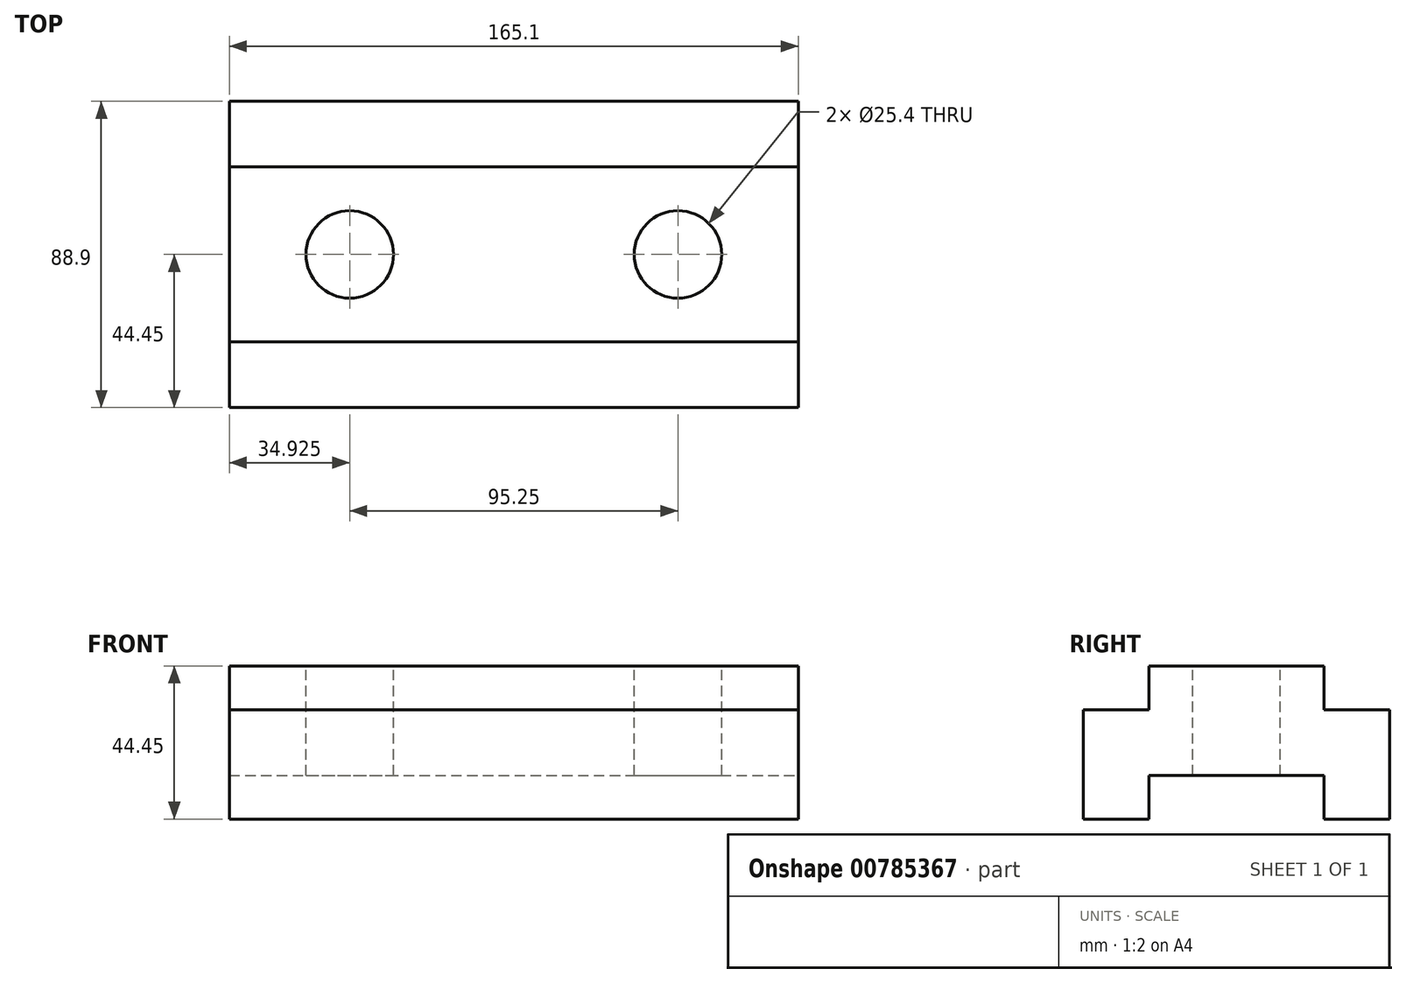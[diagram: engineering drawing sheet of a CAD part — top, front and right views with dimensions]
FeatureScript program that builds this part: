
annotation { "Feature Type Name" : "Feature", "Feature Type Description" : "" }
export const myFeature = defineFeature(function(context is Context, id is Id, definition is map)
    precondition{}
    {
        {
            var Q0;
            Q0=qCreatedBy(makeId("Right.planeOp"),FACE);
            var sketch = newSketch(context, id + "F0", { "sketchPlane" : qUnion([Q0])});
            skLineSegment(sketch, "E0", {"start": v(0, 0) * mm, "end": v(19.05, 0) * mm});
            skLineSegment(sketch, "E1", {"start": v(19.05, 0) * mm, "end": v(19.05, 12.7) * mm});
            skLineSegment(sketch, "E2", {"start": v(19.05, 12.7) * mm, "end": v(69.85, 12.7) * mm});
            skLineSegment(sketch, "E3", {"start": v(69.85, 12.7) * mm, "end": v(69.85, 0) * mm});
            skLineSegment(sketch, "E4", {"start": v(69.85, 0) * mm, "end": v(88.9, 0) * mm});
            skLineSegment(sketch, "E5", {"start": v(88.9, 0) * mm, "end": v(88.9, 31.75) * mm});
            skLineSegment(sketch, "E6", {"start": v(88.9, 31.75) * mm, "end": v(69.85, 31.75) * mm});
            skLineSegment(sketch, "E7", {"start": v(69.85, 31.75) * mm, "end": v(69.85, 44.45) * mm});
            skLineSegment(sketch, "E8", {"start": v(69.85, 44.45) * mm, "end": v(19.05, 44.45) * mm});
            skLineSegment(sketch, "E9", {"start": v(19.05, 44.45) * mm, "end": v(19.05, 31.75) * mm});
            skLineSegment(sketch, "E10", {"start": v(19.05, 31.75) * mm, "end": v(0, 31.75) * mm});
            skLineSegment(sketch, "E11", {"start": v(0, 31.75) * mm, "end": v(0, 0) * mm});
            skSolve(sketch);
        }
        {
            var Q0;
            Q0=makeQuery(id+"F0.imprint","IMPRINT",FACE,{"disambiguationData":[TD([[makeQuery(id+"F0.imprint","IMPRINT",EDGE,{"derivedFrom":sQuery(id+"F0.wireOp",EDGE,"E0")}),1.0]])]});
            extrude(context, id + "F1", {"entities" : qUnion([Q0]), "oppositeDirection" : true, "depth" : 165.1 * mm, "offsetDistance" : 25.4 * mm});
        }
        {
            var Q0;
            Q0=makeQuery(id+"F1.opExtrude","SWEPT_FACE",FACE,{"disambiguationData":[OSD([sQuery(id+"F0.wireOp",EDGE,"E8")])]});
            var sketch = newSketch(context, id + "F2", { "sketchPlane" : qUnion([Q0])});
            skLineSegment(sketch, "E12", {"start": v(-165.1, 44.45) * mm, "end": v(-130.18, 44.45) * mm, "construction": true});
            skLineSegment(sketch, "E13", {"start": v(-130.18, 44.45) * mm, "end": v(-34.92, 44.45) * mm, "construction": true});
            skCircle(sketch, "E14", {"center": v(-130.18, 44.45) * mm, "radius": 12.7 * mm});
            skCircle(sketch, "E15", {"center": v(-34.92, 44.45) * mm, "radius": 12.7 * mm});
            skSolve(sketch);
        }
        {
            var Q0;
            Q0 = qSketchRegion(id + "F2", true);
            extrude(context, id + "F3", {"entities" : qUnion([Q0]), "operationType" : NewBodyOperationType.REMOVE, "endBound" : BoundingType.UP_TO_NEXT, "oppositeDirection" : true, "depth" : 25.4 * mm, "offsetDistance" : 25.4 * mm});
        }
    });
